# Revit family: Basketball_Backstop-PSS-3104-Ceiling_Hung
name_source: partatom
category: Specialty Equipment
revit_build: Autodesk Revit 2017 (Build: 20170816_0615(x64)
units: mm (PartAtom-declared; Revit-internal decimal feet)

## family parameters
Always vertical = Yes
Cut with Voids When Loaded = No
OmniClass Number = 23.40.50.34.14.11
OmniClass Title = Backstops
Part Type = Normal
Room Calculation Point = No
Round Connector Dimension = Use Diameter
Shared = No
Work Plane-Based = No

## types (5) — shared parameters
Assembly Code = E1020900
BIM Version = v1.1
CSI MasterFormat = 11 66 23
Description = Ceiling-Hung, Rear-Fold, Rear-Braced Basketball Backstop
Installation Limitations = 30' to 40' Attachment A.F.F.
Manufacturer = Performance Sports Systems
Model = 3104
Product Page URL = http://www.perfsports.com
Superstructure Finish = Powder Coat - Performance Sports Systems - Black
URL = http://www.perfsports.com

## per-type parameters (varying)
| type | Additional Brace Centerline Dim | Dim A Rear Brace | Dim C Mast Width | Sway Brace Height |
| 30'-0" to 31'-11 7/8" | 6' - 1" | 18' - 8" | 7' - 9 1/2" | 13' - 7 1/2" |
| 32'-0" to 33'-11 7/8" | 6' - 1" | 20' - 8" | 7' - 9 1/2" | 15' - 7 1/2" |
| 34'-0" to 35'-11 7/8" | 7' - 1" | 22' - 8" | 10' - 9 1/2" | 17' - 7 1/2" |
| 36'-0" to 37'-11 7/8" | 9' - 1" | 24' - 8" | 10' - 9 1/2" | 19' - 7 1/4" |
| 38'-0" to 40'-0" | 9' - 1" | 26' - 8" | 10' - 9 1/2" | 21' - 8 3/8" |

## geometry (parser evidence)
native form markers: Blend x31, Sweep x36
no freeform markers — native parametric forms only
